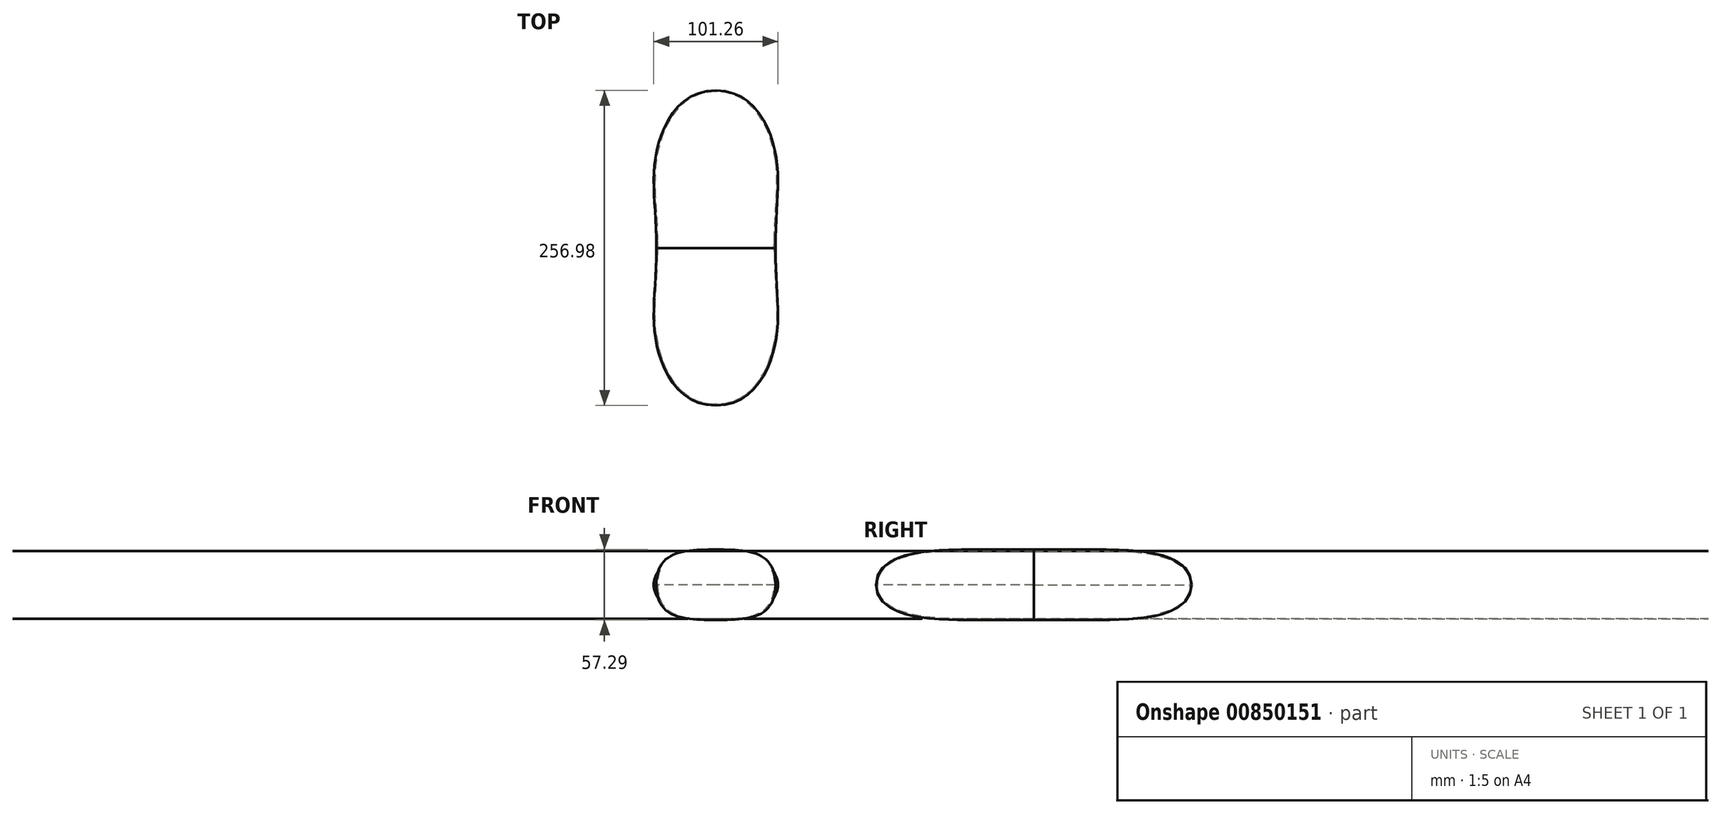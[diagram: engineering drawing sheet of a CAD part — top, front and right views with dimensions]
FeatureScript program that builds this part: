
annotation { "Feature Type Name" : "Feature", "Feature Type Description" : "" }
export const myFeature = defineFeature(function(context is Context, id is Id, definition is map)
    precondition{}
    {
        {
            var Q0;
            Q0=qCreatedBy(makeId("Front.planeOp"),FACE);
            var sketch = newSketch(context, id + "F0", { "sketchPlane" : qUnion([Q0])});
            skLineSegment(sketch, "E0.bottom", {"start": v(-48.52, 0) * mm, "end": v(48.52, 0) * mm, "construction": true});
            skLineSegment(sketch, "E0.top", {"start": v(-48.52, 28.64) * mm, "end": v(48.52, 28.64) * mm});
            skLineSegment(sketch, "E0.left", {"start": v(-48.52, 0) * mm, "end": v(-48.52, 28.64) * mm, "construction": true});
            skLineSegment(sketch, "E0.right", {"start": v(48.52, 0) * mm, "end": v(48.52, 28.64) * mm, "construction": true});
            skLineSegment(sketch, "E1", {"start": v(0, 0) * mm, "end": v(0, 28.64) * mm, "construction": true});
            skFitSpline(sketch, "E2", {"points": [v(-48.52, 28.64) * mm, v(0, 0) * mm, v(48.52, 28.64) * mm], "startDerivative": vector(0, -171.87) * mm, "endDerivative": vector(0, 171.87) * mm});
            skSolve(sketch);
        }
        {
            var Q0;
            Q0=qCreatedBy(makeId("Right.planeOp"),FACE);
            var sketch = newSketch(context, id + "F1", { "sketchPlane" : qUnion([Q0])});
            skFitSpline(sketch, "E3", {"points": [v(-128.5, 28.64) * mm, v(-52, 0) * mm, v(0, 0) * mm], "startDerivative": vector(0, -154.5) * mm, "endDerivative": vector(176.55, 0) * mm});
            skSolve(sketch);
        }
        {
            var Q0;
            Q0=sQuery(id+"F0.wireOp",EDGE,"E0.top");
            cPoint(context, id + "F2", {"entities" : qUnion([Q0]), "parameter" : 0.5});
        }
        {
            var Q0;
            Q0=qCreatedBy(makeId("Top.planeOp"),FACE);
            var Q1;
            Q1 = qCreatedBy(id + "F2" ,VERTEX);
            cPlane(context, id + "F3", {"entities" : qUnion([Q0, Q1]), "cplaneType" : CPlaneType.PLANE_POINT, "offset" : 25 * mm, "width" : 150 * mm, "height" : 150 * mm});
        }
        {
            var Q0;
            Q0=qCreatedBy(id+"F3.planeOp",FACE);
            var sketch = newSketch(context, id + "F4", { "sketchPlane" : qUnion([Q0])});
            skFitSpline(sketch, "E4", {"points": [v(48.52, 0) * mm, v(48.24, -78.9) * mm, v(0, -128.5) * mm], "startDerivative": vector(0, -197.02) * mm, "endDerivative": vector(-183.3, 0) * mm});
            skLineSegment(sketch, "E5", {"start": v(0, -128.5) * mm, "end": v(0, 0) * mm, "construction": true});
            skFitSpline(sketch, "E6.MirrorCS", {"points": [v(-48.52, 0) * mm, v(-48.24, -78.9) * mm, v(0, -128.5) * mm], "startDerivative": vector(0, -197.02) * mm, "endDerivative": vector(183.3, 0) * mm});
            skSolve(sketch);
        }
        {
            var Q0;
            Q0=makeQuery(id+"F0.imprint","IMPRINT",FACE,{"disambiguationData":[TD([[makeQuery(id+"F0.imprint","IMPRINT",EDGE,{"derivedFrom":sQuery(id+"F0.wireOp",EDGE,"E0.top")}),-1.0]])]});
            var Q1;
            Q1=sQuery(id+"F1.wireOp",VERTEX,"E3.start");
            var Q2;
            Q2=sQuery(id+"F4.wireOp",EDGE,"E4");
            var Q3;
            Q3=sQuery(id+"F1.wireOp",EDGE,"E3");
            var Q4;
            Q4=sQuery(id+"F4.wireOp",EDGE,"E6.MirrorCS");
            loft(context, id + "F5", {"addGuides" : true, "sheetProfilesArray" : [{ "sheetProfileEntities" : qUnion([Q0]) }, { "sheetProfileEntities" : qUnion([Q1]) }], "guidesArray" : [{ "guideEntities" : qUnion([Q2]), "guideDerivativeType" : LoftGuideDerivativeType.DEFAULT, "guideDerivativeMagnitude" : 1 }, { "guideEntities" : qUnion([Q3]), "guideDerivativeType" : LoftGuideDerivativeType.DEFAULT, "guideDerivativeMagnitude" : 1 }, { "guideEntities" : qUnion([Q4]), "guideDerivativeType" : LoftGuideDerivativeType.DEFAULT, "guideDerivativeMagnitude" : 1 }]});
        }
        {
            var Q0;
            Q0=makeQuery(id+"F5.opLoft","SWEPT_BODY",BODY,{"disambiguationData":[OSD([makeQuery(id+"F0.imprint","IMPRINT",FACE,{"disambiguationData":[TD([[makeQuery(id+"F0.imprint","IMPRINT",EDGE,{"derivedFrom":sQuery(id+"F0.wireOp",EDGE,"E0.top")}),-1.0]])]}),sQuery(id+"F1.wireOp",VERTEX,"E3.start"),sQuery(id+"F1.wireOp",EDGE,"E3"),sQuery(id+"F4.wireOp",EDGE,"E4"),sQuery(id+"F4.wireOp",EDGE,"E6.MirrorCS")])]});
            var Q1;
            Q1=qCreatedBy(id+"F3.planeOp",FACE);
            mirror(context, id + "F6", {"operationType" : NewBodyOperationType.ADD, "entities" : qUnion([Q0]), "mirrorPlane" : qUnion([Q1])});
        }
        {
            var Q0;
            {var subQ0=makeQuery(id+"F5.opLoft","CAP_FACE",FACE,{"disambiguationData":[OSD([makeQuery(id+"F0.imprint","IMPRINT",FACE,{"disambiguationData":[TD([[makeQuery(id+"F0.imprint","IMPRINT",EDGE,{"derivedFrom":sQuery(id+"F0.wireOp",EDGE,"E0.top")}),-1.0]])]})])],"isStart":true});Q0=makeQuery(id+"F6.boolean.opBoolean","MERGE",FACE,{"derivedFrom":[subQ0,makeQuery(id+"F6.opPattern","COPY",FACE,{"derivedFrom":subQ0,"instanceName":"1"})]});}
            shell(context, id + "F7", {"entities" : qUnion([Q0]), "thickness" : 1 * mm});
        }
        {
            var Q0;
            Q0=makeQuery(id+"F5.opLoft","SWEPT_BODY",BODY,{"disambiguationData":[OSD([makeQuery(id+"F0.imprint","IMPRINT",FACE,{"disambiguationData":[TD([[makeQuery(id+"F0.imprint","IMPRINT",EDGE,{"derivedFrom":sQuery(id+"F0.wireOp",EDGE,"E0.top")}),-1.0]])]}),sQuery(id+"F1.wireOp",VERTEX,"E3.start"),sQuery(id+"F1.wireOp",EDGE,"E3"),sQuery(id+"F4.wireOp",EDGE,"E4"),sQuery(id+"F4.wireOp",EDGE,"E6.MirrorCS")])]});
            var Q1;
            Q1=qCreatedBy(makeId("Front.planeOp"),FACE);
            mirror(context, id + "F8", {"operationType" : NewBodyOperationType.ADD, "entities" : qUnion([Q0]), "mirrorPlane" : qUnion([Q1])});
        }
    });
